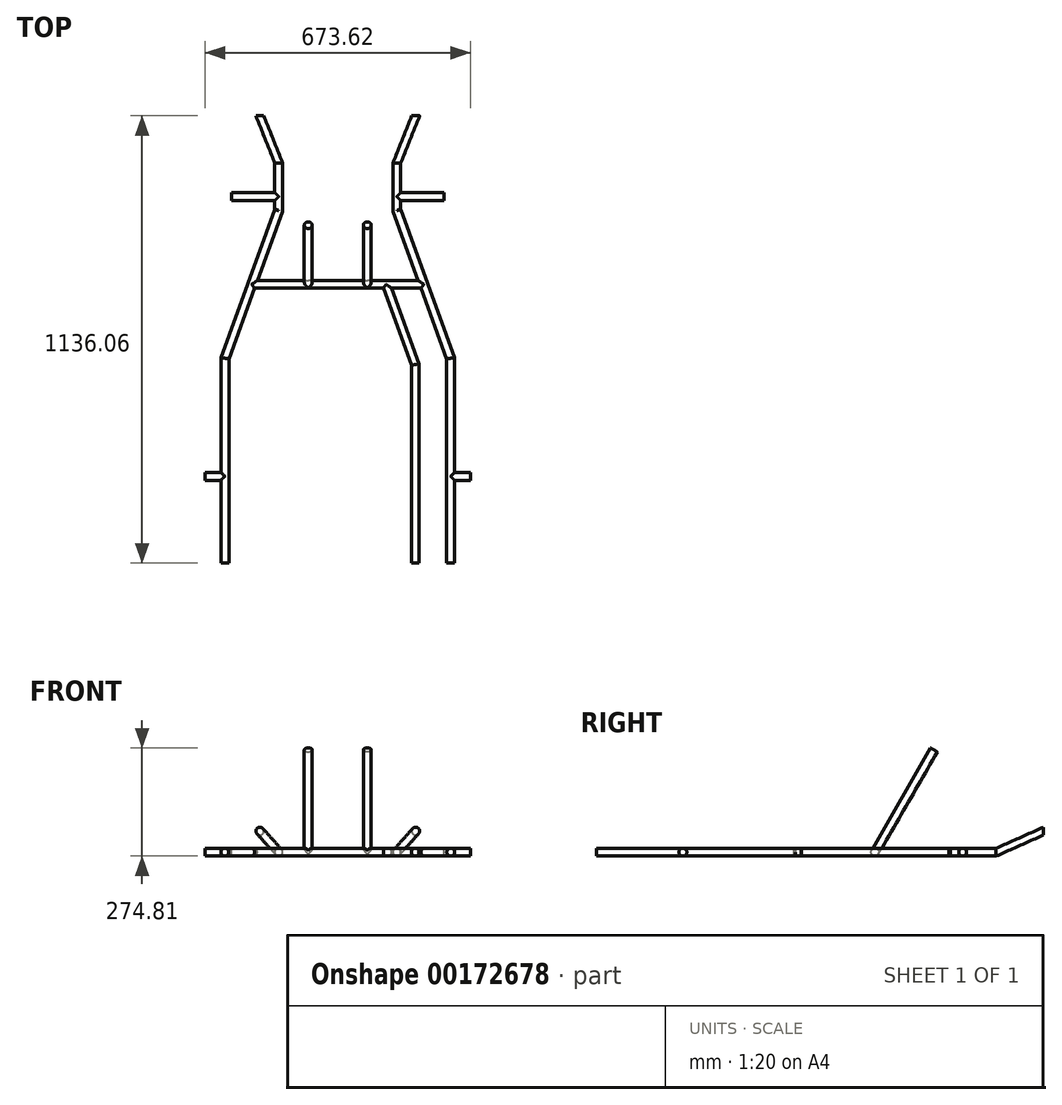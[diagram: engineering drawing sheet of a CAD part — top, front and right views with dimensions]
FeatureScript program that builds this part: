
annotation { "Feature Type Name" : "Feature", "Feature Type Description" : "" }
export const myFeature = defineFeature(function(context is Context, id is Id, definition is map)
    precondition{}
    {
        {
            var Q0;
            Q0=qCreatedBy(makeId("Top.planeOp"),FACE);
            var sketch = newSketch(context, id + "F0", { "sketchPlane" : qUnion([Q0])});
            skLineSegment(sketch, "E0", {"start": v(-150, 0) * mm, "end": v(-150, -120) * mm});
            skPoint(sketch, "E1.visualSharp", {"position": v(-150, -100) * mm});
            skLineSegment(sketch, "E2", {"start": v(-150, -120) * mm, "end": v(-286.8, -495.88) * mm});
            skLineSegment(sketch, "E3", {"start": v(-286.8, -495.88) * mm, "end": v(-286.8, -845.88) * mm});
            skLineSegment(sketch, "E4", {"start": v(-286.8, -795.88) * mm, "end": v(-336.8, -795.88) * mm});
            skLineSegment(sketch, "E5", {"start": v(-150, -85) * mm, "end": v(-270, -85) * mm});
            skLineSegment(sketch, "E6", {"start": v(-218.4, -307.94) * mm, "end": v(0, -307.94) * mm});
            skLineSegment(sketch, "E7", {"start": v(-286.8, -845.88) * mm, "end": v(-286.8, -1015.88) * mm});
            skSolve(sketch);
        }
        {
            var Q0;
            Q0=qCreatedBy(makeId("Front.planeOp"),FACE);
            var sketch = newSketch(context, id + "F1", { "sketchPlane" : qUnion([Q0])});
            skCircle(sketch, "E8", {"center": v(-150, 0) * mm, "radius": 10 * mm});
            skSolve(sketch);
        }
        {
            var Q0;
            Q0=makeQuery(id+"F1.imprint","IMPRINT",FACE,{"disambiguationData":[TD([[makeQuery(id+"F1.imprint","IMPRINT",EDGE,{"derivedFrom":sQuery(id+"F1.wireOp",EDGE,"E8")}),1.0]])]});
            var Q1;
            Q1=sQuery(id+"F1.wireOp",EDGE,"E8");
            var Q2;
            Q2=sQuery(id+"F0.wireOp",EDGE,"E2");
            var Q3;
            Q3=sQuery(id+"F0.wireOp",EDGE,"E0");
            var Q4;
            Q4=sQuery(id+"F0.wireOp",EDGE,"E3");
            var Q5;
            Q5=sQuery(id+"F0.wireOp",EDGE,"E7");
            sweep(context, id + "F2", {"profiles" : qUnion([Q0]), "surfaceProfiles" : qUnion([Q1]), "path" : qUnion([Q2, Q3, Q4, Q5])});
        }
        {
            var Q0;
            Q0=makeQuery(id+"F2.opSweep","MID_CAP_EDGE",EDGE,{"disambiguationData":[OSD([sQuery(id+"F0.wireOp",VERTEX,"E0.end"),sQuery(id+"F1.wireOp",EDGE,"E8")])],"capPos":1.0});
            fillet(context, id + "F3", {"entities" : qUnion([Q0]), "radius" : 10 * mm, "tangentPropagation" : true, "allowEdgeOverflow" : false});
        }
        {
            var Q0;
            Q0=qCreatedBy(makeId("Right.planeOp"),FACE);
            var Q1;
            Q1=sQuery(id+"F0.wireOp",VERTEX,"E4.end");
            cPlane(context, id + "F4", {"entities" : qUnion([Q0, Q1]), "cplaneType" : CPlaneType.PLANE_POINT, "offset" : 25 * mm, "width" : 150 * mm, "height" : 150 * mm});
        }
        {
            var Q0;
            Q0=qCreatedBy(id+"F4.planeOp",FACE);
            var sketch = newSketch(context, id + "F5", { "sketchPlane" : qUnion([Q0])});
            skCircle(sketch, "E9", {"center": v(-795.88, 0) * mm, "radius": 10 * mm});
            skSolve(sketch);
        }
        {
            var Q0;
            Q0=makeQuery(id+"F5.imprint","IMPRINT",FACE,{"disambiguationData":[TD([[makeQuery(id+"F5.imprint","IMPRINT",EDGE,{"derivedFrom":sQuery(id+"F5.wireOp",EDGE,"E9")}),1.0]])]});
            var Q1;
            Q1=sQuery(id+"F0.wireOp",EDGE,"E4");
            sweep(context, id + "F6", {"operationType" : NewBodyOperationType.ADD, "profiles" : qUnion([Q0]), "path" : qUnion([Q1])});
        }
        {
            var Q0;
            Q0=sQuery(id+"F0.wireOp",EDGE,"E0");
            cPoint(context, id + "F7", {"entities" : qUnion([Q0]), "parameter" : 0.5});
        }
        {
            var Q0;
            Q0=qCreatedBy(makeId("Right.planeOp"),FACE);
            var Q1;
            Q1 = qCreatedBy(id + "F7" ,VERTEX);
            cPlane(context, id + "F8", {"entities" : qUnion([Q0, Q1]), "cplaneType" : CPlaneType.PLANE_POINT, "offset" : 25 * mm, "width" : 150 * mm, "height" : 150 * mm});
        }
        {
            var Q0;
            Q0=qCreatedBy(id+"F8.planeOp",FACE);
            var sketch = newSketch(context, id + "F9", { "sketchPlane" : qUnion([Q0])});
            skCircle(sketch, "E10", {"center": v(-85, 0) * mm, "radius": 10 * mm});
            skSolve(sketch);
        }
        {
            var Q0;
            Q0 = qSketchRegion(id + "F9", true);
            var Q1;
            Q1=sQuery(id+"F0.wireOp",EDGE,"E5");
            sweep(context, id + "F10", {"operationType" : NewBodyOperationType.ADD, "profiles" : qUnion([Q0]), "path" : qUnion([Q1])});
        }
        {
            var Q0;
            Q0=qCreatedBy(makeId("Right.planeOp"),FACE);
            var sketch = newSketch(context, id + "F11", { "sketchPlane" : qUnion([Q0])});
            skCircle(sketch, "E11", {"center": v(-307.94, 0) * mm, "radius": 10 * mm});
            skSolve(sketch);
        }
        {
            var Q0;
            Q0=makeQuery(id+"F11.imprint","IMPRINT",FACE,{"disambiguationData":[TD([[makeQuery(id+"F11.imprint","IMPRINT",EDGE,{"derivedFrom":sQuery(id+"F11.wireOp",EDGE,"E11")}),1.0]])]});
            var Q1;
            Q1=sQuery(id+"F0.wireOp",EDGE,"E6");
            sweep(context, id + "F12", {"operationType" : NewBodyOperationType.ADD, "profiles" : qUnion([Q0]), "path" : qUnion([Q1])});
        }
        {
            var Q0;
            Q0=qCreatedBy(makeId("Top.planeOp"),FACE);
            var sketch = newSketch(context, id + "F13", { "sketchPlane" : qUnion([Q0])});
            skLineSegment(sketch, "E12", {"start": v(-74.15, 0) * mm, "end": v(73.31, 0) * mm, "construction": true});
            skSolve(sketch);
        }
        {
            var Q0;
            Q0=sQuery(id+"F13.wireOp",EDGE,"E12");
            var Q1;
            Q1=qCreatedBy(makeId("Top.planeOp"),FACE);
            cPlane(context, id + "F14", {"entities" : qUnion([Q0, Q1]), "cplaneType" : CPlaneType.LINE_ANGLE, "offset" : 25 * mm, "angle" : 24 * degree, "width" : 150 * mm, "height" : 150 * mm});
        }
        {
            var Q0;
            Q0=qCreatedBy(id+"F14.planeOp",FACE);
            var sketch = newSketch(context, id + "F15", { "sketchPlane" : qUnion([Q0])});
            skLineSegment(sketch, "E13", {"start": v(-150, 0) * mm, "end": v(-197.88, -131.56) * mm});
            skSolve(sketch);
        }
        {
            var Q0;
            Q0=makeQuery(id+"F2.opSweep","CAP_FACE",FACE,{"disambiguationData":[OSD([sQuery(id+"F0.wireOp",VERTEX,"E0.start"),sQuery(id+"F1.wireOp",EDGE,"E8")])],"isStart":true});
            var Q1;
            Q1=sQuery(id+"F15.wireOp",EDGE,"E13");
            sweep(context, id + "F16", {"operationType" : NewBodyOperationType.ADD, "profiles" : qUnion([Q0]), "path" : qUnion([Q1])});
        }
        {
            var Q0;
            Q0=makeQuery(id+"F2.opSweep","SWEPT_BODY",BODY,{"disambiguationData":[OSD([sQuery(id+"F0.wireOp",EDGE,"E0"),sQuery(id+"F1.wireOp",EDGE,"E8")])]});
            var Q1;
            Q1=qCreatedBy(makeId("Right.planeOp"),FACE);
            mirror(context, id + "F17", {"operationType" : NewBodyOperationType.ADD, "entities" : qUnion([Q0]), "mirrorPlane" : qUnion([Q1])});
        }
        {
            var Q0;
            Q0=qCreatedBy(makeId("Top.planeOp"),FACE);
            var sketch = newSketch(context, id + "F18", { "sketchPlane" : qUnion([Q0])});
            skLineSegment(sketch, "E14", {"start": v(196.8, -511.75) * mm, "end": v(196.8, -1015.88) * mm});
            skLineSegment(sketch, "E15", {"start": v(342.92, -1015.88) * mm, "end": v(-44.03, -1015.88) * mm, "construction": true});
            skLineSegment(sketch, "E16", {"start": v(286.8, -394.8) * mm, "end": v(286.8, -1101.3) * mm, "construction": true});
            skLineSegment(sketch, "E17", {"start": v(196.8, -511.75) * mm, "end": v(122.63, -307.94) * mm});
            skLineSegment(sketch, "E18", {"start": v(0, -307.94) * mm, "end": v(185.84, -307.94) * mm, "construction": true});
            skPoint(sketch, "E19", {"position": v(92.92, -307.94) * mm});
            skLineSegment(sketch, "E20", {"start": v(286.8, -495.88) * mm, "end": v(219, -309.57) * mm, "construction": true});
            skSolve(sketch);
        }
        {
            var Q0;
            Q0=qCreatedBy(makeId("Front.planeOp"),FACE);
            var Q1;
            Q1=sQuery(id+"F18.wireOp",VERTEX,"E14.end");
            cPlane(context, id + "F19", {"entities" : qUnion([Q0, Q1]), "cplaneType" : CPlaneType.PLANE_POINT, "offset" : 25 * mm, "width" : 150 * mm, "height" : 150 * mm});
        }
        {
            var Q0;
            Q0=qCreatedBy(id+"F19.planeOp",FACE);
            var sketch = newSketch(context, id + "F20", { "sketchPlane" : qUnion([Q0])});
            skCircle(sketch, "E21", {"center": v(196.8, 0) * mm, "radius": 10 * mm});
            skSolve(sketch);
        }
        {
            var Q0;
            Q0=makeQuery(id+"F20.imprint","IMPRINT",FACE,{"disambiguationData":[TD([[makeQuery(id+"F20.imprint","IMPRINT",EDGE,{"derivedFrom":sQuery(id+"F20.wireOp",EDGE,"E21")}),1.0]])]});
            var Q1;
            Q1=sQuery(id+"F18.wireOp",EDGE,"E14");
            var Q2;
            Q2=sQuery(id+"F18.wireOp",EDGE,"E17");
            sweep(context, id + "F21", {"operationType" : NewBodyOperationType.ADD, "profiles" : qUnion([Q0]), "path" : qUnion([Q1, Q2])});
        }
        {
            var Q0;
            Q0=sQuery(id+"F0.wireOp",EDGE,"E6");
            cPlane(context, id + "F22", {"entities" : qUnion([Q0]), "cplaneType" : CPlaneType.LINE_ANGLE, "offset" : 25 * mm, "angle" : 150 * degree, "width" : 150 * mm, "height" : 150 * mm});
        }
        {
            var Q0;
            Q0=qCreatedBy(id+"F22.planeOp",FACE);
            var sketch = newSketch(context, id + "F23", { "sketchPlane" : qUnion([Q0])});
            skLineSegment(sketch, "E22", {"start": v(0, -153.97) * mm, "end": v(0, -100.6) * mm, "construction": true});
            skLineSegment(sketch, "E23", {"start": v(-75, -143.97) * mm, "end": v(-75, 156.03) * mm});
            skSolve(sketch);
        }
        {
            var Q0;
            Q0=sQuery(id+"F0.wireOp",EDGE,"E6");
            cPlane(context, id + "F24", {"entities" : qUnion([Q0]), "cplaneType" : CPlaneType.LINE_ANGLE, "offset" : 25 * mm, "angle" : 240 * degree, "width" : 150 * mm, "height" : 150 * mm});
        }
        {
            var Q0;
            Q0=qCreatedBy(id+"F24.planeOp",FACE);
            cPlane(context, id + "F25", {"entities" : qUnion([Q0]), "cplaneType" : CPlaneType.OFFSET, "offset" : 0 * mm, "width" : 150 * mm, "height" : 150 * mm});
        }
        {
            var Q0;
            Q0=qCreatedBy(id+"F25.planeOp",FACE);
            var sketch = newSketch(context, id + "F26", { "sketchPlane" : qUnion([Q0])});
            skCircle(sketch, "E24", {"center": v(-75, 266.68) * mm, "radius": 10 * mm});
            skSolve(sketch);
        }
        {
            var Q0;
            Q0=makeQuery(id+"F26.imprint","IMPRINT",FACE,{"disambiguationData":[TD([[makeQuery(id+"F26.imprint","IMPRINT",EDGE,{"derivedFrom":sQuery(id+"F26.wireOp",EDGE,"E24")}),1.0]])]});
            var Q1;
            Q1=sQuery(id+"F23.wireOp",EDGE,"E23");
            sweep(context, id + "F27", {"profiles" : qUnion([Q0]), "path" : qUnion([Q1])});
        }
        {
            var Q0;
            Q0=makeQuery(id+"F27.opSweep","SWEPT_BODY",BODY,{"disambiguationData":[OSD([sQuery(id+"F23.wireOp",EDGE,"E23"),sQuery(id+"F26.wireOp",EDGE,"E24")])]});
            var Q1;
            Q1=qCreatedBy(makeId("Right.planeOp"),FACE);
            mirror(context, id + "F28", {"operationType" : NewBodyOperationType.ADD, "entities" : qUnion([Q0]), "mirrorPlane" : qUnion([Q1])});
        }
    });
